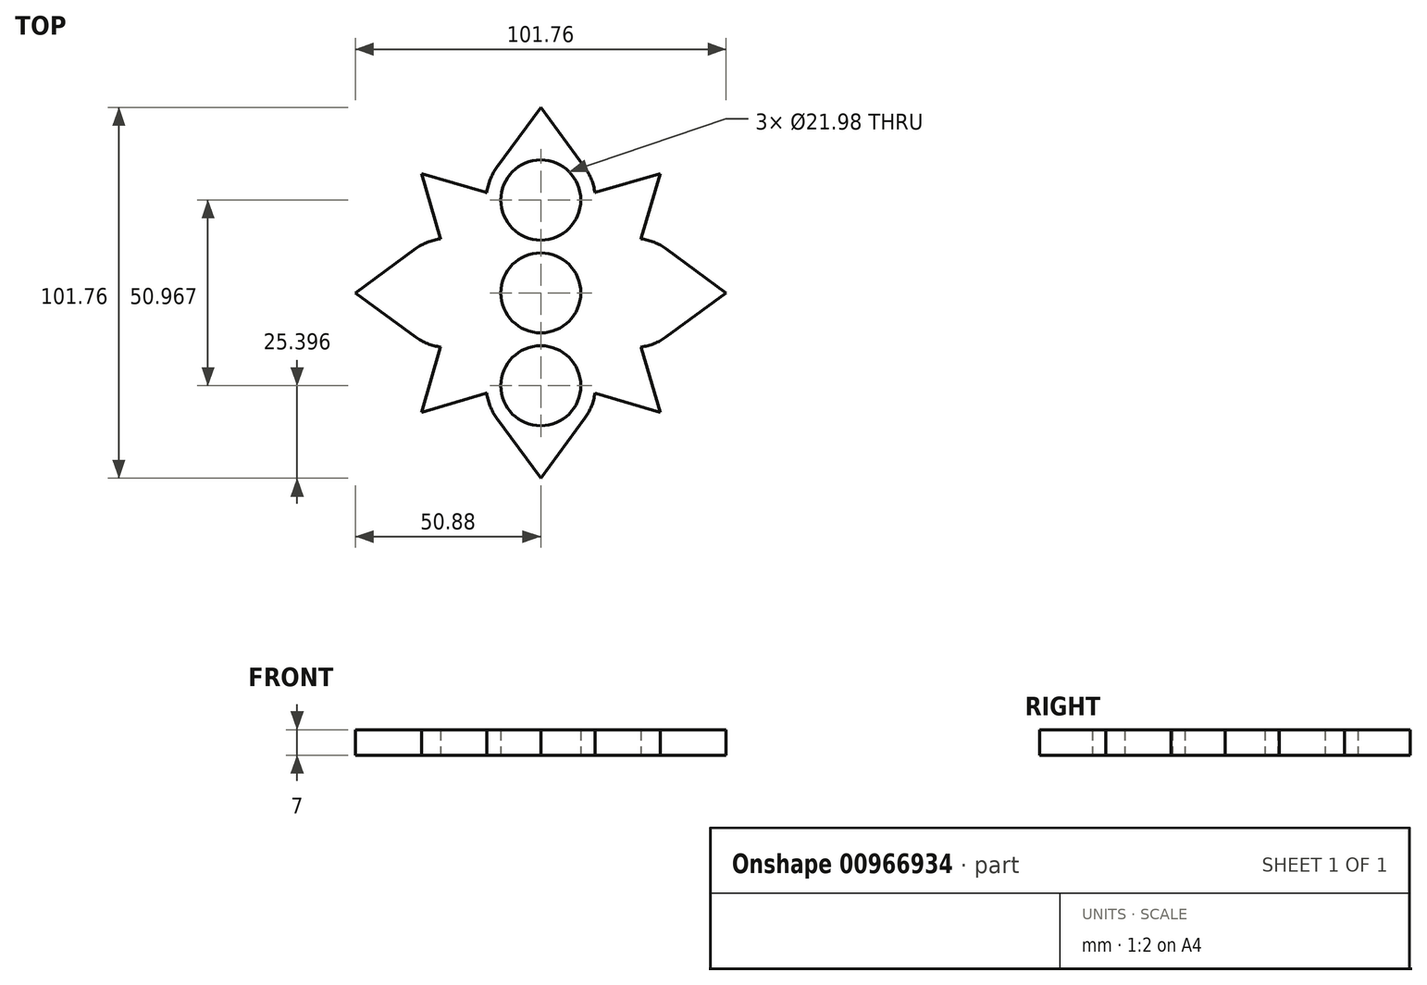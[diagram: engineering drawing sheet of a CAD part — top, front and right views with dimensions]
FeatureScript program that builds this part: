
annotation { "Feature Type Name" : "Feature", "Feature Type Description" : "" }
export const myFeature = defineFeature(function(context is Context, id is Id, definition is map)
    precondition{}
    {
        {
            var Q0;
            Q0=qCreatedBy(makeId("Top.planeOp"),FACE);
            var sketch = newSketch(context, id + "F0", { "sketchPlane" : qUnion([Q0])});
            skCircle(sketch, "E0", {"center": v(0, 0) * mm, "radius": 11 * mm});
            skCircle(sketch, "E1", {"center": v(0, 25.48) * mm, "radius": 11 * mm});
            skCircle(sketch, "E2", {"center": v(0, -25.48) * mm, "radius": 11 * mm});
            skLineSegment(sketch, "E3", {"start": v(0, 25.48) * mm, "end": v(0, -25.48) * mm, "construction": true});
            skLineSegment(sketch, "E4.bottom", {"start": v(-29.85, 57.15) * mm, "end": v(29.85, 57.15) * mm, "construction": true});
            skLineSegment(sketch, "E4.top", {"start": v(-29.85, -57.15) * mm, "end": v(29.85, -57.15) * mm, "construction": true});
            skLineSegment(sketch, "E4.left", {"start": v(-29.84, 57.15) * mm, "end": v(-29.85, -57.15) * mm, "construction": true});
            skLineSegment(sketch, "E4.right", {"start": v(29.85, 57.15) * mm, "end": v(29.84, -57.15) * mm, "construction": true});
            skPoint(sketch, "E5", {"position": v(0, 57.15) * mm});
            skPoint(sketch, "E6", {"position": v(-29.85, 0) * mm});
            skSolve(sketch);
        }
        {
            var Q0;
            Q0=qCreatedBy(makeId("Top.planeOp"),FACE);
            var sketch = newSketch(context, id + "F1", { "sketchPlane" : qUnion([Q0])});
            skCircle(sketch, "E7", {"center": v(0, 25.48) * mm, "radius": 11 * mm});
            skCircle(sketch, "E8", {"center": v(0, 0) * mm, "radius": 11 * mm});
            skCircle(sketch, "E9", {"center": v(0, -25.48) * mm, "radius": 11 * mm});
            skLineSegment(sketch, "E10.bottom", {"start": v(-29.85, 57.15) * mm, "end": v(29.84, 57.15) * mm, "construction": true});
            skLineSegment(sketch, "E10.top", {"start": v(-29.85, -57.15) * mm, "end": v(29.84, -57.15) * mm, "construction": true});
            skLineSegment(sketch, "E10.left", {"start": v(-29.85, 57.15) * mm, "end": v(-29.85, -57.15) * mm, "construction": true});
            skLineSegment(sketch, "E10.right", {"start": v(29.85, 57.15) * mm, "end": v(29.85, -57.15) * mm, "construction": true});
            skPoint(sketch, "E11", {"position": v(-29.85, 0) * mm});
            skPoint(sketch, "E12", {"position": v(0, 57.15) * mm});
            skArc(sketch, "E13", {"start": v(14.86, 27.5) * mm, "mid": v(13.91, 31.1) * mm, "end": v(12.1, 34.34) * mm});
            skLineSegment(sketch, "E14", {"start": v(-12.1, 34.34) * mm, "end": v(0, 50.88) * mm});
            skLineSegment(sketch, "E15", {"start": v(0, 50.88) * mm, "end": v(12.1, 34.34) * mm});
            skLineSegment(sketch, "E16.1.0", {"start": v(-34.34, -12.1) * mm, "end": v(-50.88, 0) * mm});
            skLineSegment(sketch, "E16.1.1", {"start": v(-50.88, 0) * mm, "end": v(-34.34, 12.1) * mm});
            skArc(sketch, "E16.1.2", {"start": v(-27.5, 14.86) * mm, "mid": v(-31.1, 13.91) * mm, "end": v(-34.34, 12.1) * mm});
            skLineSegment(sketch, "E16.2.0", {"start": v(12.1, -34.34) * mm, "end": v(0, -50.88) * mm});
            skLineSegment(sketch, "E16.2.1", {"start": v(0, -50.88) * mm, "end": v(-12.1, -34.34) * mm});
            skArc(sketch, "E16.2.2", {"start": v(-14.86, -27.5) * mm, "mid": v(-13.91, -31.1) * mm, "end": v(-12.1, -34.34) * mm});
            skLineSegment(sketch, "E16.3.0", {"start": v(34.34, 12.1) * mm, "end": v(50.88, 0) * mm});
            skLineSegment(sketch, "E16.3.1", {"start": v(50.88, 0) * mm, "end": v(34.34, -12.1) * mm});
            skArc(sketch, "E16.3.2", {"start": v(27.5, -14.86) * mm, "mid": v(31.1, -13.91) * mm, "end": v(34.34, -12.1) * mm});
            skLineSegment(sketch, "E17", {"start": v(0, 0) * mm, "end": v(7.77, 7.77) * mm, "construction": true});
            skLineSegment(sketch, "E18", {"start": v(25.48, 0) * mm, "end": v(0, 0) * mm, "construction": true});
            skLineSegment(sketch, "E19", {"start": v(0, 0) * mm, "end": v(0, 25.48) * mm, "construction": true});
            skArc(sketch, "E20", {"start": v(27.5, 14.86) * mm, "mid": v(27.56, 15.04) * mm, "end": v(27.62, 15.21) * mm});
            skLineSegment(sketch, "E21", {"start": v(15.21, 27.62) * mm, "end": v(32.75, 32.75) * mm});
            skLineSegment(sketch, "E22", {"start": v(32.75, 32.75) * mm, "end": v(27.62, 15.21) * mm});
            skLineSegment(sketch, "E23", {"start": v(18.02, 18.02) * mm, "end": v(32.75, 32.75) * mm, "construction": true});
            skArc(sketch, "E24.1.0", {"start": v(-27.62, 15.21) * mm, "mid": v(-27.56, 15.04) * mm, "end": v(-27.5, 14.86) * mm});
            skLineSegment(sketch, "E24.1.1", {"start": v(-32.75, 32.75) * mm, "end": v(-15.21, 27.62) * mm});
            skLineSegment(sketch, "E24.1.2", {"start": v(-27.62, 15.21) * mm, "end": v(-32.75, 32.75) * mm});
            skArc(sketch, "E24.2.0", {"start": v(-27.5, -14.86) * mm, "mid": v(-27.56, -15.04) * mm, "end": v(-27.62, -15.21) * mm});
            skLineSegment(sketch, "E24.2.1", {"start": v(-32.75, -32.75) * mm, "end": v(-27.62, -15.21) * mm});
            skLineSegment(sketch, "E24.2.2", {"start": v(-15.21, -27.62) * mm, "end": v(-32.75, -32.75) * mm});
            skArc(sketch, "E24.3.0", {"start": v(14.86, -27.5) * mm, "mid": v(15.04, -27.56) * mm, "end": v(15.21, -27.62) * mm});
            skLineSegment(sketch, "E24.3.1", {"start": v(32.75, -32.75) * mm, "end": v(15.21, -27.62) * mm});
            skLineSegment(sketch, "E24.3.2", {"start": v(27.62, -15.21) * mm, "end": v(32.75, -32.75) * mm});
            skArc(sketch, "E25.trimOffspring", {"start": v(27.62, -15.21) * mm, "mid": v(27.56, -15.04) * mm, "end": v(27.5, -14.86) * mm});
            skArc(sketch, "E26.trimOffspring", {"start": v(-12.1, 34.34) * mm, "mid": v(-13.91, 31.1) * mm, "end": v(-14.86, 27.5) * mm});
            skArc(sketch, "E27.trimOffspring", {"start": v(-14.86, 27.5) * mm, "mid": v(-15.04, 27.56) * mm, "end": v(-15.21, 27.62) * mm});
            skArc(sketch, "E28.trimOffspring", {"start": v(12.1, -34.34) * mm, "mid": v(13.91, -31.1) * mm, "end": v(14.86, -27.5) * mm});
            skArc(sketch, "E29.trimOffspring", {"start": v(-15.21, -27.62) * mm, "mid": v(-15.04, -27.56) * mm, "end": v(-14.86, -27.5) * mm});
            skArc(sketch, "E30.trimOffspring", {"start": v(-34.34, -12.1) * mm, "mid": v(-31.1, -13.91) * mm, "end": v(-27.5, -14.86) * mm});
            skArc(sketch, "E31.trimOffspring", {"start": v(34.34, 12.1) * mm, "mid": v(31.1, 13.91) * mm, "end": v(27.5, 14.86) * mm});
            skArc(sketch, "E32.trimOffspring", {"start": v(15.21, 27.62) * mm, "mid": v(15.04, 27.56) * mm, "end": v(14.86, 27.5) * mm});
            skSolve(sketch);
        }
        {
            var Q0;
            Q0 = qSketchRegion(id + "F1", true);
            extrude(context, id + "F2", {"entities" : qUnion([Q0]), "depth" : 7 * mm, "offsetDistance" : 25.4 * mm});
        }
    });
